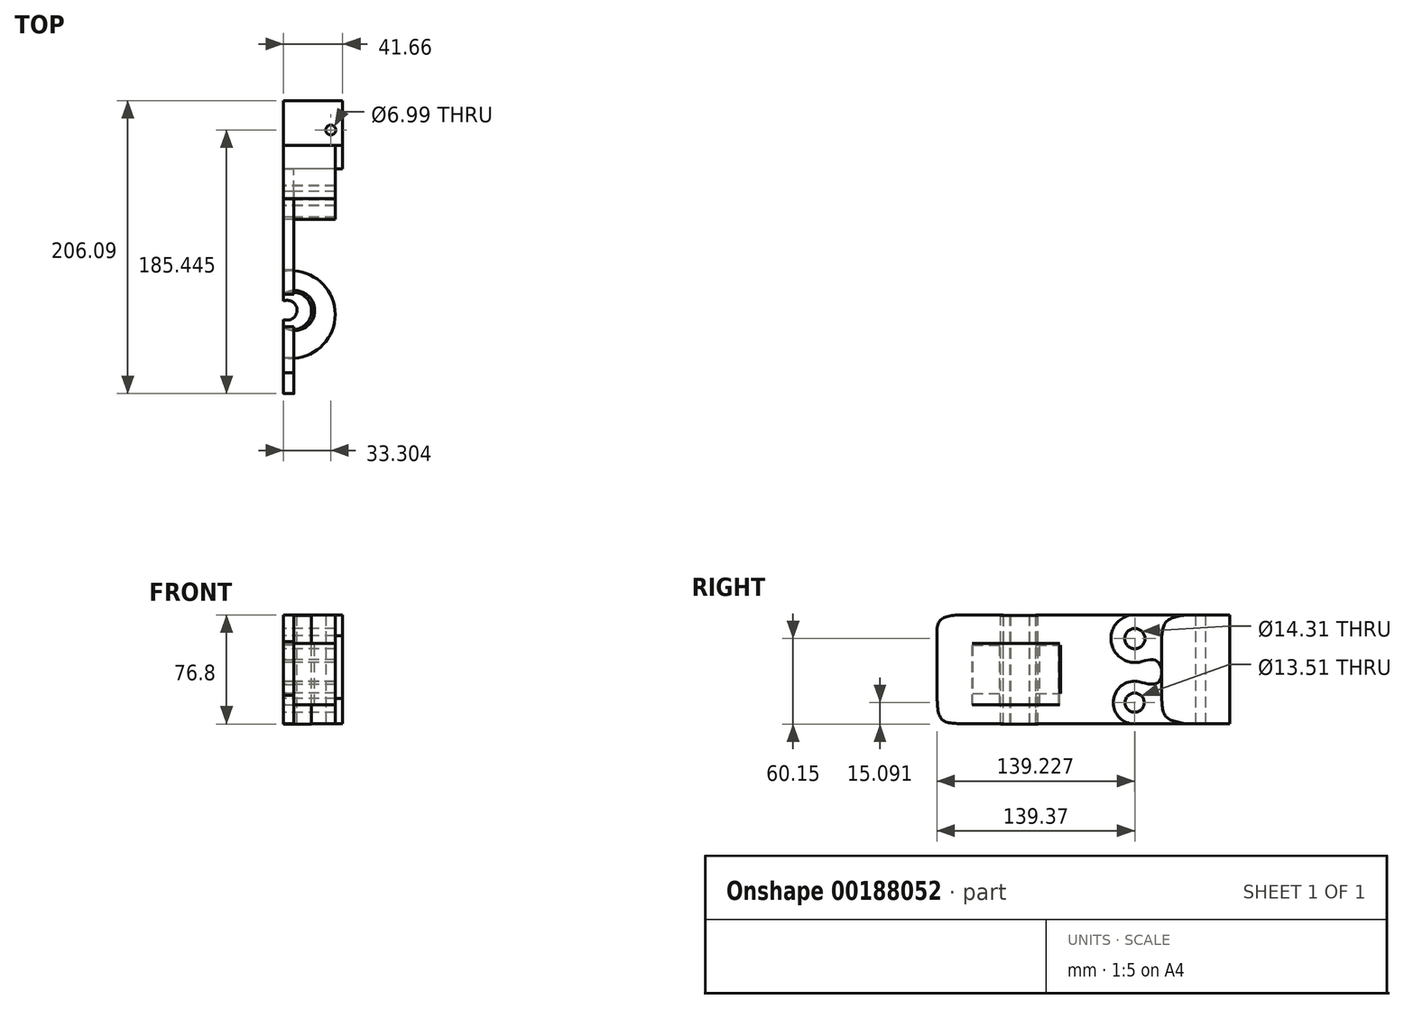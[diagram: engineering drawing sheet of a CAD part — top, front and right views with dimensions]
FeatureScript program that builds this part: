
annotation { "Feature Type Name" : "Feature", "Feature Type Description" : "" }
export const myFeature = defineFeature(function(context is Context, id is Id, definition is map)
    precondition{}
    {
        {
            var Q0;
            Q0=qCreatedBy(makeId("Right.planeOp"),FACE);
            var sketch = newSketch(context, id + "F0", { "sketchPlane" : qUnion([Q0])});
            skLineSegment(sketch, "E0.bottom", {"start": v(-12.03, 37.94) * mm, "end": v(124.28, 37.94) * mm});
            skLineSegment(sketch, "E0.right", {"start": v(124.28, 37.94) * mm, "end": v(124.28, -38.52) * mm});
            skLineSegment(sketch, "E1", {"start": v(-12.03, 37.94) * mm, "end": v(-34.94, 37.94) * mm});
            skLineSegment(sketch, "E2.bottom", {"start": v(-56.7, 16.75) * mm, "end": v(5.15, 16.75) * mm});
            skLineSegment(sketch, "E2.top", {"start": v(-56.7, -17.33) * mm, "end": v(5.15, -17.33) * mm});
            skLineSegment(sketch, "E2.left", {"start": v(-56.7, 16.75) * mm, "end": v(-56.7, -17.33) * mm});
            skLineSegment(sketch, "E2.right", {"start": v(5.15, 16.75) * mm, "end": v(5.15, -17.33) * mm});
            skLineSegment(sketch, "E3", {"start": v(-34.94, 37.94) * mm, "end": v(-67.3, 37.94) * mm});
            skLineSegment(sketch, "E4", {"start": v(-34.94, -38.52) * mm, "end": v(-67.3, -38.52) * mm});
            skFitSpline(sketch, "E5", {"points": [v(-67.3, 37.94) * mm, v(-79.61, 33.93) * mm, v(-81.62, 19.04) * mm], "startDerivative": vector(-30.8, -3.42) * mm, "endDerivative": vector(1.76, -34) * mm});
            skLineSegment(sketch, "E6", {"start": v(-81.62, 19.04) * mm, "end": v(-81.62, -18.76) * mm});
            skFitSpline(sketch, "E7", {"points": [v(-67.3, -38.52) * mm, v(-78.47, -35.37) * mm, v(-81.62, -18.76) * mm], "startDerivative": vector(-28.93, 1.65) * mm, "endDerivative": vector(-0.6, 36.77) * mm});
            skArc(sketch, "E8", {"start": v(59.85, 37.94) * mm, "mid": v(40.75, 21) * mm, "end": v(60.42, 4.73) * mm});
            skArc(sketch, "E9", {"start": v(60.42, -9.02) * mm, "mid": v(42.37, -23.77) * mm, "end": v(60.42, -38.52) * mm});
            skFitSpline(sketch, "E10", {"points": [v(76.46, 23.34) * mm, v(79.9, 33.36) * mm, v(92.78, 37.94) * mm], "startDerivative": vector(3.39, 24.4) * mm, "endDerivative": vector(28.72, 5.21) * mm});
            skLineSegment(sketch, "E11", {"start": v(76.46, 23.34) * mm, "end": v(76.46, -20.76) * mm});
            skFitSpline(sketch, "E12", {"points": [v(76.46, -20.76) * mm, v(79.61, -33.65) * mm, v(92.78, -38.52) * mm], "startDerivative": vector(1.56, -30.22) * mm, "endDerivative": vector(30.94, -5.4) * mm});
            skFitSpline(sketch, "E13", {"points": [v(60.42, 4.73) * mm, v(74.07, 4.73) * mm, v(74.65, -9.02) * mm, v(60.42, -9.02) * mm], "startDerivative": vector(48.91, 13.75) * mm, "endDerivative": vector(-51.27, 13.92) * mm});
            skCircle(sketch, "E14", {"center": v(57.56, 21.3) * mm, "radius": 7.15 * mm});
            skCircle(sketch, "E15", {"center": v(57.42, -23.77) * mm, "radius": 6.76 * mm});
            skCircle(sketch, "E16", {"center": v(57.56, 21.3) * mm, "radius": 4.33 * mm});
            skCircle(sketch, "E17", {"center": v(57.42, -23.77) * mm, "radius": 4.32 * mm});
            skLineSegment(sketch, "E18", {"start": v(-34.94, 37.94) * mm, "end": v(-34.94, 16.75) * mm});
            skLineSegment(sketch, "E19", {"start": v(-12.03, 37.94) * mm, "end": v(-12.03, 16.75) * mm});
            skLineSegment(sketch, "E20", {"start": v(-34.94, -38.52) * mm, "end": v(-34.94, -17.33) * mm});
            skLineSegment(sketch, "E21", {"start": v(-34.94, -38.52) * mm, "end": v(124.28, -38.52) * mm});
            skLineSegment(sketch, "E22", {"start": v(-12.03, -17.33) * mm, "end": v(-12.03, -38.52) * mm});
            skSolve(sketch);
        }
        {
            var Q0;
            {var subQ0=sQuery(id+"F0.wireOp",EDGE,"E0.right");Q0=makeQuery(id+"F0.imprint","IMPRINT",FACE,{"disambiguationData":[TD([[makeQuery(id+"F0.imprint","IMPRINT",EDGE,{"derivedFrom":subQ0}),-1.0]])]});}
            extrude(context, id + "F1", {"entities" : qUnion([Q0]), "depth" : 41.66 * mm});
        }
        {
            var Q0;
            {var subQ9=sQuery(id+"F0.wireOp",EDGE,"E2.right");Q0=makeQuery(id+"F0.imprint","IMPRINT",FACE,{"disambiguationData":[TD([[makeQuery(id+"F0.imprint","IMPRINT",EDGE,{"derivedFrom":subQ9}),1.0]])]});}
            var Q1;
            {var subQ0=sQuery(id+"F0.wireOp",EDGE,"E2.left");Q1=makeQuery(id+"F0.imprint","IMPRINT",FACE,{"disambiguationData":[TD([[makeQuery(id+"F0.imprint","IMPRINT",EDGE,{"derivedFrom":subQ0}),-1.0]])]});}
            extrude(context, id + "F2", {"entities" : qUnion([Q0, Q1]), "depth" : 7.37 * mm});
        }
        {
            var Q0;
            {var subQ0=sQuery(id+"F0.wireOp",EDGE,"E10");Q0=makeQuery(id+"F0.imprint","IMPRINT",FACE,{"disambiguationData":[TD([[makeQuery(id+"F0.imprint","IMPRINT",EDGE,{"derivedFrom":subQ0}),1.0]])]});}
            extrude(context, id + "F3", {"entities" : qUnion([Q0]), "depth" : 36.58 * mm});
        }
        {
            var Q0;
            Q0=makeQuery(id+"F1.opExtrude","SWEPT_FACE",FACE,{"disambiguationData":[OSD([sQuery(id+"F0.wireOp",EDGE,"E21")])]});
            cPlane(context, id + "F4", {"entities" : qUnion([Q0]), "cplaneType" : CPlaneType.OFFSET, "offset" : 0.25 * mm, "width" : 152.4 * mm, "height" : 152.4 * mm});
        }
        {
            var Q0;
            Q0=qCreatedBy(id+"F4.planeOp",FACE);
            var sketch = newSketch(context, id + "F5", { "sketchPlane" : qUnion([Q0])});
            skCircle(sketch, "E23", {"center": v(33.3, -103.64) * mm, "radius": 3.5 * mm});
            skSolve(sketch);
        }
        {
            var Q0;
            Q0=makeQuery(id+"F5.imprint","IMPRINT",FACE,{"disambiguationData":[TD([[makeQuery(id+"F5.imprint","IMPRINT",EDGE,{"derivedFrom":sQuery(id+"F5.wireOp",EDGE,"E23")}),1.0]])]});
            extrude(context, id + "F6", {"entities" : qUnion([Q0]), "operationType" : NewBodyOperationType.REMOVE, "oppositeDirection" : true, "depth" : 76.96 * mm});
        }
        {
            var Q0;
            Q0=qCreatedBy(makeId("Top.planeOp"),FACE);
            cPlane(context, id + "F7", {"entities" : qUnion([Q0]), "cplaneType" : CPlaneType.OFFSET, "offset" : 17.78 * mm, "width" : 152.4 * mm, "height" : 152.4 * mm});
        }
        {
            var Q0;
            Q0=qCreatedBy(id+"F7.planeOp",FACE);
            var sketch = newSketch(context, id + "F8", { "sketchPlane" : qUnion([Q0])});
            skArc(sketch, "E24", {"start": v(0, -56.46) * mm, "mid": v(36.4, -26.22) * mm, "end": v(0, 4.03) * mm});
            skArc(sketch, "E25", {"start": v(0, -35.06) * mm, "mid": v(21.97, -23.4) * mm, "end": v(0, -11.75) * mm});
            skLineSegment(sketch, "E26", {"start": v(0, -56.46) * mm, "end": v(0, -35.06) * mm});
            skLineSegment(sketch, "E27", {"start": v(0, -11.75) * mm, "end": v(0, 4.03) * mm});
            skSolve(sketch);
        }
        {
            var Q0;
            Q0=qCreatedBy(makeId("Top.planeOp"),FACE);
            cPlane(context, id + "F9", {"entities" : qUnion([Q0]), "cplaneType" : CPlaneType.OFFSET, "offset" : 37.6 * mm, "width" : 152.4 * mm, "height" : 152.4 * mm});
        }
        {
            var Q0;
            Q0=qCreatedBy(id+"F9.planeOp",FACE);
            var sketch = newSketch(context, id + "F10", { "sketchPlane" : qUnion([Q0])});
            skArc(sketch, "E28", {"start": v(0, -29.71) * mm, "mid": v(9.54, -23.2) * mm, "end": v(0, -16.69) * mm});
            skLineSegment(sketch, "E29", {"start": v(0, -35.08) * mm, "end": v(0, -29.71) * mm});
            skLineSegment(sketch, "E30", {"start": v(0, -16.69) * mm, "end": v(0, -12.26) * mm});
            skArc(sketch, "E31", {"start": v(0, -35.08) * mm, "mid": v(19.8, -23.67) * mm, "end": v(0, -12.26) * mm});
            skSolve(sketch);
        }
        {
            var Q0;
            Q0=makeQuery(id+"F8.imprint","IMPRINT",FACE,{"disambiguationData":[TD([[makeQuery(id+"F8.imprint","IMPRINT",EDGE,{"derivedFrom":sQuery(id+"F8.wireOp",EDGE,"E24")}),1.0]])]});
            extrude(context, id + "F11", {"entities" : qUnion([Q0]), "oppositeDirection" : true, "depth" : 43.18 * mm});
        }
        {
            var Q0;
            Q0=makeQuery(id+"F10.imprint","IMPRINT",FACE,{"disambiguationData":[TD([[makeQuery(id+"F10.imprint","IMPRINT",EDGE,{"derivedFrom":sQuery(id+"F10.wireOp",EDGE,"E28")}),-1.0]])]});
            extrude(context, id + "F12", {"entities" : qUnion([Q0]), "oppositeDirection" : true, "depth" : 76.45 * mm});
        }
    });
